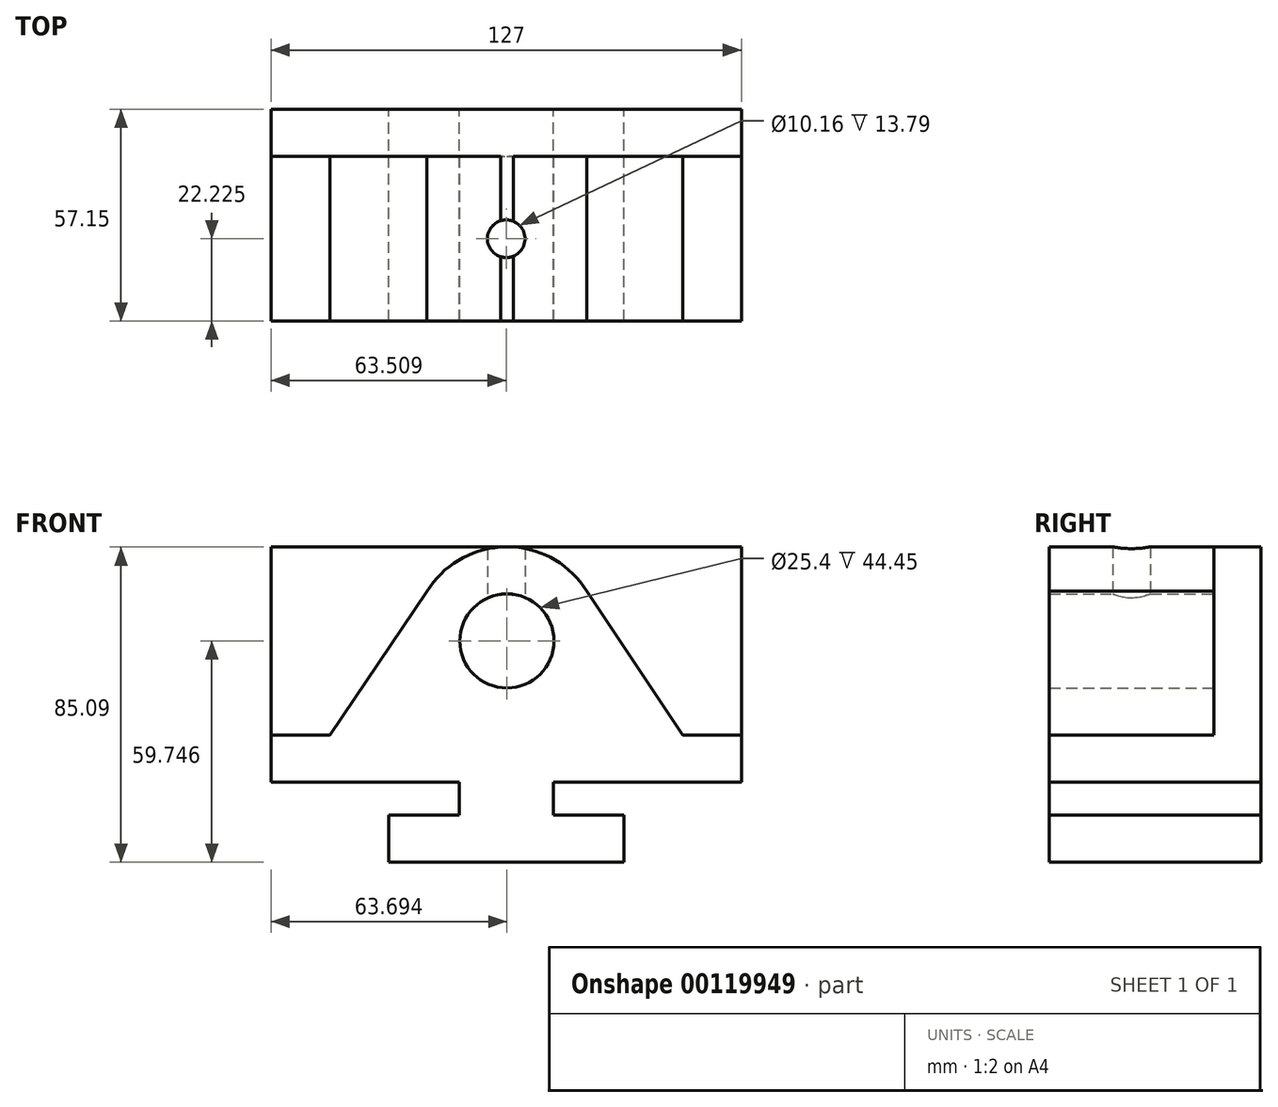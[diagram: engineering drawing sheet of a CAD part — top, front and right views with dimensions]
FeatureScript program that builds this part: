
annotation { "Feature Type Name" : "Feature", "Feature Type Description" : "" }
export const myFeature = defineFeature(function(context is Context, id is Id, definition is map)
    precondition{}
    {
        {
            var Q0;
            Q0=qCreatedBy(makeId("Front.planeOp"),FACE);
            var sketch = newSketch(context, id + "F0", { "sketchPlane" : qUnion([Q0])});
            skLineSegment(sketch, "E0", {"start": v(76.2, -8.9) * mm, "end": v(76.2, 0) * mm});
            skLineSegment(sketch, "E1", {"start": v(76.2, 0) * mm, "end": v(127, 0) * mm});
            skLineSegment(sketch, "E2", {"start": v(127, 0) * mm, "end": v(127, 63.5) * mm});
            skLineSegment(sketch, "E3", {"start": v(127, 63.5) * mm, "end": v(0, 63.5) * mm});
            skLineSegment(sketch, "E4", {"start": v(0, 63.5) * mm, "end": v(0, 0) * mm});
            skLineSegment(sketch, "E5", {"start": v(0, 0) * mm, "end": v(50.8, 0) * mm});
            skLineSegment(sketch, "E6", {"start": v(50.8, 0) * mm, "end": v(50.8, -8.89) * mm});
            skLineSegment(sketch, "E7", {"start": v(50.8, -8.9) * mm, "end": v(31.75, -8.9) * mm});
            skLineSegment(sketch, "E8", {"start": v(31.75, -8.9) * mm, "end": v(31.75, -21.59) * mm});
            skLineSegment(sketch, "E9", {"start": v(31.75, -21.59) * mm, "end": v(95.25, -21.59) * mm});
            skLineSegment(sketch, "E10", {"start": v(95.25, -21.59) * mm, "end": v(95.25, -8.89) * mm});
            skLineSegment(sketch, "E11", {"start": v(95.25, -8.89) * mm, "end": v(76.2, -8.89) * mm});
            skSolve(sketch);
        }
        {
            var Q0;
            Q0 = qSketchRegion(id + "F0", true);
            extrude(context, id + "F1", {"entities" : qUnion([Q0]), "depth" : 57.15 * mm});
        }
        {
            var Q0;
            Q0=qCreatedBy(makeId("Front.planeOp"),FACE);
            var sketch = newSketch(context, id + "F2", { "sketchPlane" : qUnion([Q0])});
            skLineSegment(sketch, "E12.top", {"start": v(0, 63.5) * mm, "end": v(127, 63.5) * mm});
            skLineSegment(sketch, "E12.left", {"start": v(0, 12.7) * mm, "end": v(0, 63.5) * mm});
            skLineSegment(sketch, "E12.right", {"start": v(127, 12.7) * mm, "end": v(127, 63.5) * mm});
            skLineSegment(sketch, "E13.top", {"start": v(0, 12.7) * mm, "end": v(15.88, 12.7) * mm});
            skLineSegment(sketch, "E14", {"start": v(111.12, 12.7) * mm, "end": v(127, 12.7) * mm});
            skLineSegment(sketch, "E15", {"start": v(0, 12.7) * mm, "end": v(15.87, 12.7) * mm});
            skArc(sketch, "E16", {"start": v(85.2, 51.67) * mm, "mid": v(63.59, 63.56) * mm, "end": v(42.07, 51.49) * mm});
            skLineSegment(sketch, "E17", {"start": v(15.87, 12.7) * mm, "end": v(42.07, 51.49) * mm});
            skLineSegment(sketch, "E18", {"start": v(85.2, 51.67) * mm, "end": v(111.12, 12.7) * mm});
            skCircle(sketch, "E19", {"center": v(63.7, 38.16) * mm, "radius": 12.7 * mm});
            skSolve(sketch);
        }
        {
            var Q0;
            Q0 = qSketchRegion(id + "F2", true);
            extrude(context, id + "F3", {"entities" : qUnion([Q0]), "operationType" : NewBodyOperationType.REMOVE, "depth" : 57.15 * mm, "hasSecondDirection" : true, "secondDirectionOppositeDirection" : false, "secondDirectionDepth" : 12.7 * mm});
        }
        {
            var Q0;
            Q0=qCreatedBy(makeId("Top.planeOp"),FACE);
            var sketch = newSketch(context, id + "F4", { "sketchPlane" : qUnion([Q0])});
            skCircle(sketch, "E20", {"center": v(63.5, -34.93) * mm, "radius": 5.08 * mm});
            skLineSegment(sketch, "E21", {"start": v(127.15, -12.7) * mm, "end": v(127.15, 0) * mm, "construction": true});
            skLineSegment(sketch, "E22", {"start": v(127.15, -12.7) * mm, "end": v(127.15, -57.15) * mm, "construction": true});
            skSolve(sketch);
        }
        {
            var Q0;
            Q0 = qSketchRegion(id + "F4", true);
            extrude(context, id + "F5", {"entities" : qUnion([Q0]), "operationType" : NewBodyOperationType.REMOVE, "depth" : 90.95 * mm, "hasSecondDirection" : true, "secondDirectionOppositeDirection" : false, "secondDirectionDepth" : 48.52 * mm});
        }
    });
